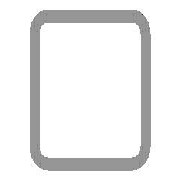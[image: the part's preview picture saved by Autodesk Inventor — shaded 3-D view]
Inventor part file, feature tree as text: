
AUTODESK INVENTOR PART (.ipt)
format: ipt  version: 2018 (Build 220112000, 112)  size: 158,720 bytes
history: native  units: mm (DEFAULTED — no unit token found)
features: sketch x5, other x3, extrude x2, hole x1, plane x1
ambient origin geometry x8: Origin, YZ Plane, XZ Plane, XY Plane, X Axis, Y Axis, Z Axis, Center Point
bodies: Solid1 (feature_tree)
feature tree (12):
  other  "Driven Length"
  other  "Piano iniziale"
  other  "Piano finale"
  extrude  "Corpo"  TaperAngle=0.0deg  [1 undecoded]
  extrude  "Estrusione2"  Depth=20.0mm
  hole  "Foro1"  [1 undecoded]
  sketch  "Schizzo"
  sketch  "Sketch3"  dims[d3=200.0mm d4=0.0mm]
  plane  "Work Plane3"
  sketch  "Sketch4"  dims[d7=4.0mm d9=20.0mm d11=20.0mm d12=2.0mm d13=-0.0mm d14=200.0mm d15=10.0mm d16=10.0mm d17=90.0deg d18=200.0mm d19=45.0deg d20=45.0deg d21=10.0mm d22=0.0mm d23=10.0mm d24=10.0mm d25=6.0mm d26=4.0mm d27=2.0mm d28=90.0deg d29=8.0mm d30=20.594885mm]
  sketch  "Schizzo5"
  sketch  "Schizzo6"
note: 2 required parameter values undecoded (feature->parameter linkage not recoverable at this tier; creation-order binding heuristic only, values carry confidence <= 0.55)
